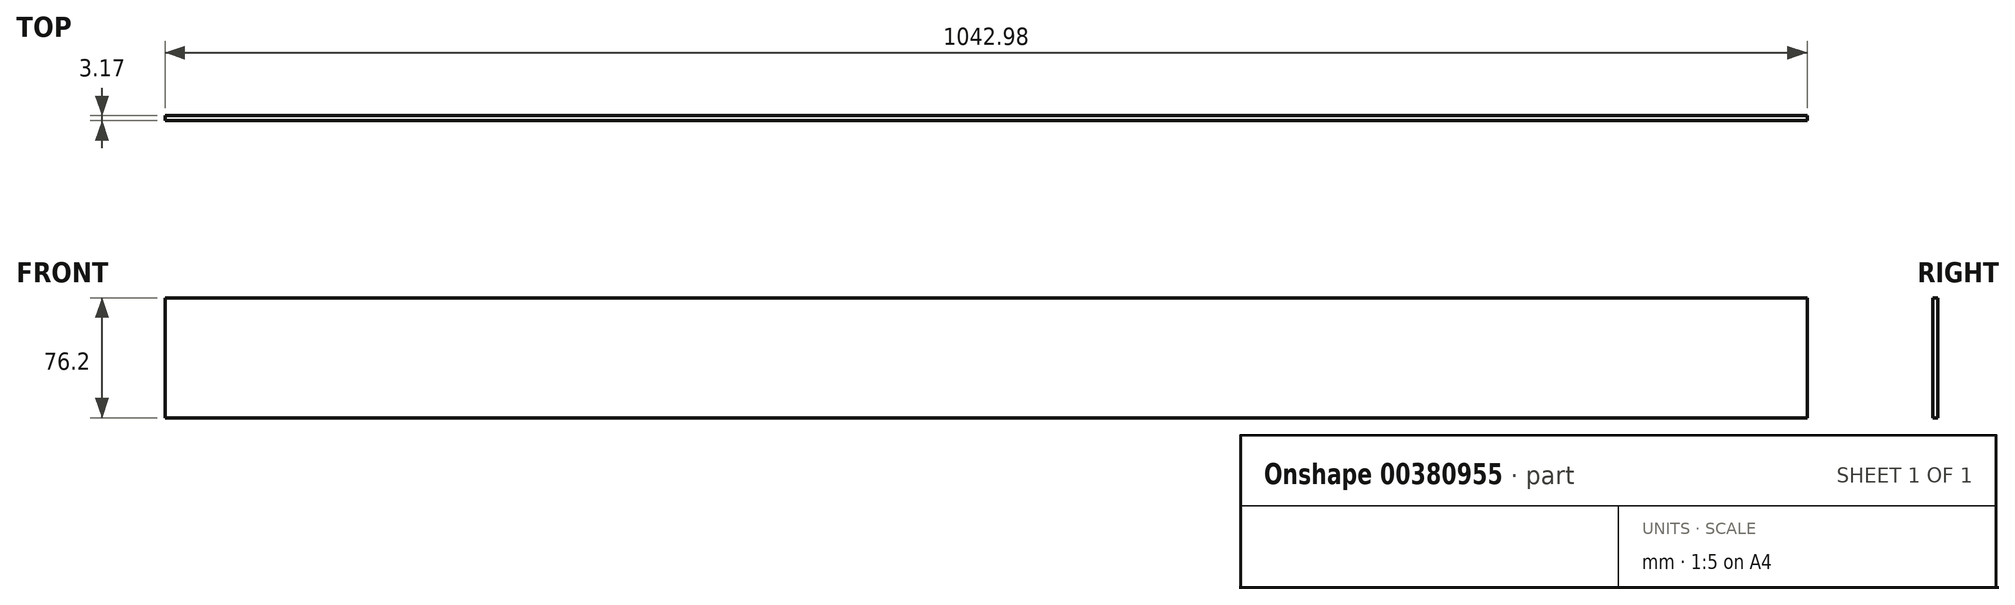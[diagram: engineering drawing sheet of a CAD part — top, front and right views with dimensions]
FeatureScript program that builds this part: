
annotation { "Feature Type Name" : "Feature", "Feature Type Description" : "" }
export const myFeature = defineFeature(function(context is Context, id is Id, definition is map)
    precondition{}
    {
        {
            var Q0;
            Q0=qCreatedBy(makeId("Front.planeOp"),FACE);
            var sketch = newSketch(context, id + "F0", { "sketchPlane" : qUnion([Q0])});
            skLineSegment(sketch, "E0.bottom", {"start": v(521.5, 38.1) * mm, "end": v(-521.5, 38.1) * mm});
            skLineSegment(sketch, "E0.top", {"start": v(521.5, -38.1) * mm, "end": v(-521.5, -38.1) * mm});
            skLineSegment(sketch, "E0.left", {"start": v(521.5, 38.1) * mm, "end": v(521.5, -38.1) * mm});
            skLineSegment(sketch, "E0.right", {"start": v(-521.5, 38.1) * mm, "end": v(-521.5, -38.1) * mm});
            skPoint(sketch, "E0.middle", {"position": v(0, 0) * mm});
            skSolve(sketch);
        }
        {
            var Q0;
            Q0=qSketchRegion(id+"F0",true);
            extrude(context, id + "F1", {"entities" : qUnion([Q0]), "depth" : 3.17 * mm});
        }
    });
